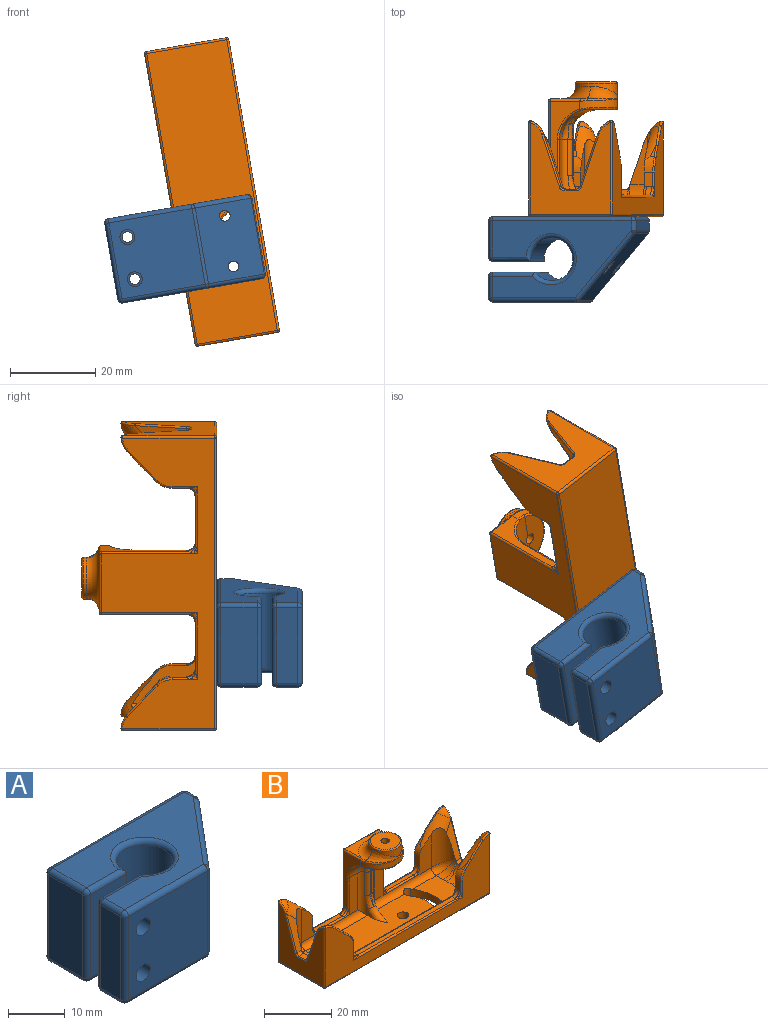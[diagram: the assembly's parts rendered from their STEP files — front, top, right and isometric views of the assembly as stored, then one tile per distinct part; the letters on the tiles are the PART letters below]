
ASSEMBLY  parts=2 mates=1
PART A: 56 faces, bbox 35.6x20.6x20.6 mm
  f0: plane 18x5.02mm, normal (-1,0,0), area 90.4mm2, adj f44,f49,f52,f55
  f1: plane 19.74x18mm, normal (0,-1,0), area 336mm2, adj f13,f14,f41,f50,f51,f55
  f2: plane 18.63x16.41mm, normal (0.77,-0.64,0), area 355.8mm2, adj f15,f16,f32,f40,f41,f42
  f3: plane 18x2.22mm, normal (1,0,0), area 40mm2, adj f22,f31,f32,f33
  f4: plane 33x18mm, normal (0,1,0), area 574.4mm2, adj f11,f12,f15,f16,f17,f21,f22,f23
  f5: plane 18x8.48mm, normal (-1,0,0), area 152.6mm2, adj f17,f20,f24,f25
  f6: plane 18x9.02mm, normal (0,-1,0), area 152.6mm2, adj f7,f11,f12,f25,f30,f34
  f7: cylinder r=5mm len=18mm, axis (0,0,-1), area 516.7mm2, adj f6,f8,f35,f38
  f8: plane 18x9.98mm, normal (0,1,0), area 160.5mm2, adj f7,f13,f14,f39,f43,f44
  f9: plane 33x18mm, normal (0,0,1), area 338.4mm2, adj f20,f21,f30,f31,f35,f39,f40,f49
  f10: plane 33x18mm, normal (0,0,-1), area 338.4mm2, adj f23,f24,f33,f34,f38,f42,f43,f51
  f11: cylinder r=1.25mm len=10.48mm, axis (0,-1,0), area 82.3mm2, adj f4,f6
  f12: cylinder r=1.25mm len=10.48mm, axis (0,-1,0), area 82.3mm2, adj f4,f6
  f13: cylinder r=1.75mm len=7.02mm, axis (0,-1,0), area 77.2mm2, adj f1,f8
  f14: cylinder r=1.75mm len=7.02mm, axis (0,-1,0), area 77.2mm2, adj f1,f8
  f15: cylinder r=1.25mm len=13.4mm, axis (0,1,0), area 93.6mm2, adj f2,f4
  f16: cylinder r=1.25mm len=13.4mm, axis (0,1,0), area 93.6mm2, adj f2,f4
  f17: cylinder r=1mm len=18mm, axis (0,0,1), area 28.3mm2, adj f4,f5,f18,f19
  f18: sphere r=1mm, area 1.6mm2, adj f17,f20,f21
  f19: sphere r=1mm, area 1.6mm2, adj f17,f23,f24
  f20: cylinder r=1mm len=8.48mm, axis (0,1,0), area 13.3mm2, adj f5,f9,f18,f26
  f21: cylinder r=1mm len=33mm, axis (1,0,0), area 51.8mm2, adj f4,f9,f18,f27
  f22: cylinder r=1mm len=18mm, axis (0,0,-1), area 28.3mm2, adj f3,f4,f27,f28
  f23: cylinder r=1mm len=33mm, axis (-1,0,0), area 51.8mm2, adj f4,f10,f19,f28
  f24: cylinder r=1mm len=8.48mm, axis (0,-1,0), area 13.3mm2, adj f5,f10,f19,f29
  f25: cylinder r=1mm len=18mm, axis (0,0,-1), area 28.3mm2, adj f5,f6,f26,f29
  f26: sphere r=1mm, area 1.6mm2, adj f20,f25,f30
  f27: sphere r=1mm, area 1.6mm2, adj f21,f22,f31
  f28: sphere r=1mm, area 1.6mm2, adj f22,f23,f33
  f29: sphere r=1mm, area 1.6mm2, adj f24,f25,f34
  f30: cylinder r=1mm len=9.02mm, axis (-1,0,0), area 13.4mm2, adj f6,f9,f26,f35
  f31: cylinder r=1mm len=2.22mm, axis (0,-1,0), area 3.5mm2, adj f3,f9,f27,f36
  f32: cylinder r=1mm len=18mm, axis (0,0,1), area 12.6mm2, adj f2,f3,f36,f37
  f33: cylinder r=1mm len=2.22mm, axis (0,1,0), area 3.5mm2, adj f3,f10,f28,f37
  f34: cylinder r=1mm len=9.02mm, axis (1,0,0), area 13.4mm2, adj f6,f10,f29,f38
  f35: torus R=6mm, axis (0,0,1), area 47.2mm2, adj f7,f9,f30,f39
  f36: sphere r=1mm, area 1mm2, adj f31,f32,f40
  f37: sphere r=1mm, area 1mm2, adj f32,f33,f42
  f38: torus R=6mm, axis (0,0,1), area 47.2mm2, adj f7,f10,f34,f43
  f39: cylinder r=1mm len=9.98mm, axis (1,0,0), area 15.3mm2, adj f8,f9,f35,f45
  f40: cylinder r=1mm len=16.42mm, axis (-0.64,-0.77,0), area 32.4mm2, adj f2,f9,f36,f46
  f41: cylinder r=1mm len=18mm, axis (0,0,-1), area 15.7mm2, adj f1,f2,f46,f47
  f42: cylinder r=1mm len=16.42mm, axis (0.64,0.77,0), area 32.4mm2, adj f2,f10,f37,f47
  f43: cylinder r=1mm len=9.98mm, axis (-1,0,0), area 15.3mm2, adj f8,f10,f38,f48
  f44: cylinder r=1mm len=18mm, axis (0,0,1), area 28.3mm2, adj f0,f8,f45,f48
  f45: sphere r=1mm, area 1.6mm2, adj f39,f44,f49
  f46: sphere r=1mm, area 0.6mm2, adj f40,f41,f50
  f47: sphere r=1mm, area 0.9mm2, adj f41,f42,f51
  f48: sphere r=1mm, area 1.6mm2, adj f43,f44,f52
  f49: cylinder r=1mm len=5.02mm, axis (0,1,0), area 7.9mm2, adj f0,f9,f45,f53
  f50: cylinder r=1mm len=19.74mm, axis (-1,0,0), area 31mm2, adj f1,f9,f46,f53
  f51: cylinder r=1mm len=19.74mm, axis (1,0,0), area 31mm2, adj f1,f10,f47,f54
  f52: cylinder r=1mm len=5.02mm, axis (0,-1,0), area 7.9mm2, adj f0,f10,f48,f54
  f53: sphere r=1mm, area 1.6mm2, adj f49,f50,f55
  f54: sphere r=1mm, area 1.6mm2, adj f51,f52,f55
  f55: cylinder r=1mm len=18mm, axis (0,0,-1), area 28.3mm2, adj f0,f1,f53,f54
PART B: 212 faces, bbox 74x22.6x33.9 mm
  f0: cylinder r=2mm len=2mm, axis (0,-1,0), area 3.9mm2, adj f28,f31,f208,f209
  f1: cylinder r=2mm len=2mm, axis (0,1,0), area 3.9mm2, adj f30,f35,f206,f207
  f2: cylinder r=2mm len=2mm, axis (0,-1,0), area 3mm2, adj f3,f27,f37,f211
  f3: bspline ~2.19x2.14mm, area 2mm2, adj f2,f8,f27,f37,f137,f192
  f4: cylinder r=2mm len=2mm, axis (0,1,0), area 3mm2, adj f5,f28,f38,f210
  f5: bspline ~2.17x2.17mm, area 1.9mm2, adj f4,f7,f28,f38,f119,f122
  f6: bspline ~1.67x1.66mm, area 0.8mm2, adj f125,f128,f211
  f7: bspline ~1.84x1.84mm, area 0.8mm2, adj f5,f119,f122
  f8: bspline ~1.72x1.68mm, area 0.7mm2, adj f3,f137,f192
  f9: bspline ~1.72x1.68mm, area 0.7mm2, adj f134,f198,f210
  f10: bspline ~1.72x1.68mm, area 0.7mm2, adj f119,f191,f209
  f11: bspline ~1.72x1.68mm, area 0.7mm2, adj f135,f150,f207
  f12: bspline ~1.72x1.68mm, area 0.7mm2, adj f135,f171,f205
  f13: bspline ~1.72x1.68mm, area 0.7mm2, adj f125,f170,f202
  f14: plane 13.5x3.6mm, normal (0,-1,0), area 48.6mm2, adj f58,f60,f61,f192
  f15: plane 12.4x7.12mm, normal (0,-1,0), area 51.8mm2, adj f31,f62,f89,f97,f99,f208
  f16: plane 12x10.12mm, normal (0,0,1), area 100.1mm2, adj f62,f83,f84,f85,f86,f87,f111,f114
  f17: plane 0.3x0.1mm, normal (-1,0,0), area 0mm2, adj f43,f87,f89
  f18: plane 11.44x4.12mm, normal (1,0,0), area 24.5mm2, adj f40,f76,f102,f113
  f19: plane 12.4x7.12mm, normal (0,-1,0), area 51.8mm2, adj f34,f60,f82,f103,f104,f200
  f20: plane 44.84x12.37mm, normal (0,0,1), area 492.7mm2, adj f55,f56,f60,f62,f71,f76,f77,f78
  f21: plane 69x26.5mm, normal (0,1,0), area 899.8mm2, adj f119,f122,f125,f128,f129,f143,f147,f149
  f22: plane 21.43x19mm, normal (-1,0,0), area 244.6mm2, adj f140,f146,f149,f156,f157,f158,f159,f160
  f23: plane 69x21.46mm, normal (0,-1,0), area 584.8mm2, adj f135,f138,f140,f141,f150,f151,f152,f153
  f24: plane 21.43x19mm, normal (1,0,0), area 244.6mm2, adj f138,f142,f143,f177,f178,f179,f180,f181
  f25: plane 69x19mm, normal (0,0,-1), area 1255.1mm2, adj f114,f115,f116,f117,f118,f141,f142,f146
  f26: plane 13.5x3.6mm, normal (0,-1,0), area 48.6mm2, adj f58,f62,f64,f198
  f27: plane 11.03x1.53mm, normal (0,0,1), area 16.5mm2, adj f2,f3,f125,f137,f201,f202,f211
  f28: plane 11.03x1.53mm, normal (0,0,1), area 16.5mm2, adj f0,f4,f5,f119,f134,f209,f210
  f29: plane 63x16.19mm, normal (0,1,0), area 270.1mm2, adj f32,f35,f94,f95,f100,f102,f109,f110
  f30: plane 41x1.5mm, normal (0,0,1), area 61.5mm2, adj f1,f135,f136,f204,f205,f207
  f31: plane 3.52x2.14mm, normal (-1,0,0), area 7.2mm2, adj f0,f15,f97,f191,f208,f209
  f32: plane 3.52x2.14mm, normal (-1,0,0), area 7.2mm2, adj f29,f94,f171,f203,f204,f205
  f33: plane 11.44x4.12mm, normal (-1,0,0), area 24.5mm2, adj f45,f83,f95,f109
  f34: plane 3.52x2.14mm, normal (1,0,0), area 7.2mm2, adj f19,f103,f170,f200,f201,f202
  f35: plane 3.52x2.14mm, normal (1,0,0), area 7.2mm2, adj f1,f29,f100,f150,f206,f207
  f36: plane 0.3x0.1mm, normal (1,0,0), area 0mm2, adj f42,f80,f82
  f37: plane 20.04x7.04mm, normal (-1,0,0), area 52.2mm2, adj f2,f3,f50,f128,f133,f192,f193,f211
  f38: plane 20.14x7.04mm, normal (1,0,0), area 52.2mm2, adj f4,f5,f50,f120,f121,f122,f123,f197
  f39: plane 14x7.02mm, normal (0,0,1), area 39.9mm2, adj f106,f123,f129,f132,f133
  f40: plane 12.88x4.42mm, normal (0,0.95,0.32), area 24.6mm2, adj f18,f77,f78,f91,f102,f158
  f41: plane 2.57x2.1mm, normal (0,0,1), area 5.4mm2, adj f78,f90,f91,f160
  f42: plane 12.99x4.53mm, normal (0,-0.95,0.32), area 27.6mm2, adj f36,f78,f79,f82,f90,f104,f162
  f43: plane 12.99x4.53mm, normal (0,-0.95,0.32), area 27.6mm2, adj f17,f85,f86,f89,f92,f99,f183
  f44: plane 2.57x2.1mm, normal (0,0,1), area 5.4mm2, adj f85,f92,f93,f181
  f45: plane 12.88x4.42mm, normal (0,0.95,0.32), area 24.6mm2, adj f33,f84,f85,f93,f95,f179
  f46: plane 13.63x5.1mm, normal (0,0,-1), area 47.5mm2, adj f48,f58,f195
  f47: cylinder r=4.9mm len=9.8mm, axis (0,0,-1), area 37.4mm2, adj f106,f107,f108,f199
  f48: cylinder r=1.25mm len=6.5mm, axis (0,0,-1), area 51.1mm2, adj f46,f49,f58
  f49: plane 9x9mm, normal (0,0,1), area 58.7mm2, adj f48,f199
  f50: cylinder r=7.5mm len=15mm, axis (0,0,1), area 44.4mm2, adj f37,f38,f124,f127,f130,f132,f194,f195
  f51: plane 2.72x2.72mm, normal (-0.71,0,0.71), area 1.8mm2, adj f94,f95,f173
  f52: plane 2.72x2.72mm, normal (-0.71,0,0.71), area 1.8mm2, adj f97,f99,f189
  f53: plane 2.72x2.72mm, normal (0.71,0,0.71), area 1.8mm2, adj f100,f102,f152
  f54: plane 2.72x2.72mm, normal (0.71,0,0.71), area 1.8mm2, adj f103,f104,f168
  f55: plane 2.18x2.18mm, normal (-1,0,0), area 2.1mm2, adj f20,f61,f71
  f56: plane 2.18x2.18mm, normal (1,0,0), area 2.1mm2, adj f20,f64,f71
  f57: plane 12.5x2.39mm, normal (0,-1,0), area 10.4mm2, adj f59,f65,f68,f69,f73,f74
  f58: cylinder r=7mm len=14.2mm, axis (-1,0,0), area 108.9mm2, adj f14,f26,f46,f48,f63,f65,f66,f193
  f59: cylinder r=7mm len=3.97mm, axis (-1,0,0), area 1.4mm2, adj f57,f70,f72
  f60: cylinder r=2mm len=26mm, axis (1,0,0), area 78.5mm2, adj f14,f19,f20,f61,f81,f137
  f61: cylinder r=2mm len=15.5mm, axis (0,0,1), area 35.9mm2, adj f14,f55,f60,f63,f72,f73
  f62: cylinder r=2mm len=26mm, axis (1,0,0), area 76.1mm2, adj f15,f16,f20,f26,f64,f88,f115,f116
  f63: torus R=5mm, axis (1,0,0), area 8.7mm2, adj f58,f61,f74,f75
  f64: cylinder r=2mm len=15.5mm, axis (0,0,-1), area 35.9mm2, adj f26,f56,f62,f66,f69,f70
  f65: cylinder r=2mm len=7mm, axis (-1,0,0), area 8.7mm2, adj f57,f58,f67,f75
  f66: torus R=5mm, axis (1,0,0), area 8.7mm2, adj f58,f64,f67,f68
  f67: bspline ~2.42x2.34mm, area 1.2mm2, adj f65,f66,f68
  f68: bspline ~5.73x2.08mm, area 5.9mm2, adj f57,f66,f67,f69
  f69: cylinder r=1.5mm len=8.5mm, axis (0,0,-1), area 14.4mm2, adj f57,f64,f68,f70
  f70: bspline ~7.01x2.35mm, area 8.6mm2, adj f59,f64,f69,f71
  f71: torus R=8.5mm, axis (1,0,0), area 23.3mm2, adj f20,f55,f56,f70,f72
  f72: bspline ~6.14x2.35mm, area 8.6mm2, adj f59,f61,f71,f73
  f73: cylinder r=1.5mm len=8.5mm, axis (0,0,1), area 14.4mm2, adj f57,f61,f72,f74
  f74: bspline ~5.33x2.08mm, area 5.9mm2, adj f57,f63,f73,f75
  f75: bspline ~2.8x2.75mm, area 1.2mm2, adj f63,f65,f74
  f76: cylinder r=5mm len=5mm, axis (0,1,0), area 32.2mm2, adj f18,f20,f77,f112
  f77: bspline ~5.08x5.07mm, area 7.3mm2, adj f20,f40,f76,f78
  f78: cylinder r=5mm len=4.98mm, axis (0,-1,0), area 21.5mm2, adj f20,f40,f41,f42,f77,f79,f90,f91
  f79: bspline ~5x5mm, area 7.5mm2, adj f20,f42,f78,f80
  f80: cylinder r=5mm len=5mm, axis (0,1,0), area 15.8mm2, adj f20,f36,f79,f81
  f81: bspline ~5.23x5mm, area 10.8mm2, adj f60,f80,f82
  f82: cylinder r=5mm len=13.53mm, axis (0,0,-1), area 77.4mm2, adj f19,f36,f42,f81,f104
  f83: cylinder r=5mm len=5mm, axis (0,-1,0), area 32.2mm2, adj f16,f33,f84,f110
  f84: bspline ~5.08x5.07mm, area 7.3mm2, adj f16,f45,f83,f85
  f85: cylinder r=5mm len=4.98mm, axis (0,-1,0), area 21.5mm2, adj f16,f43,f44,f45,f84,f86,f92,f93
  f86: bspline ~5x5mm, area 7.5mm2, adj f16,f43,f85,f87
  f87: cylinder r=5mm len=5mm, axis (0,-1,0), area 15.8mm2, adj f16,f17,f86,f88
  f88: bspline ~5.91x5mm, area 10.8mm2, adj f62,f87,f89
  f89: cylinder r=5mm len=13.53mm, axis (0,0,1), area 77.4mm2, adj f15,f17,f43,f88,f99
  f90: cylinder r=1mm len=2.1mm, axis (-1,0,0), area 2.5mm2, adj f41,f42,f78,f161
  f91: cylinder r=1mm len=2.1mm, axis (1,0,0), area 2.5mm2, adj f40,f41,f78,f159
  f92: cylinder r=1mm len=2.1mm, axis (-1,0,0), area 2.5mm2, adj f43,f44,f85,f182
  f93: cylinder r=1mm len=2.1mm, axis (1,0,0), area 2.5mm2, adj f44,f45,f85,f180
  f94: cylinder r=5mm len=3.54mm, axis (0,-1,0), area 7.7mm2, adj f29,f32,f51,f95,f172
  f95: cylinder r=5mm len=11.54mm, axis (0.69,-0.23,0.69), area 27.7mm2, adj f29,f33,f45,f51,f94,f96,f109,f174
  f96: sphere r=5mm, area 7.8mm2, adj f95,f175,f176,f177
  f97: cylinder r=5mm len=3.54mm, axis (0,-1,0), area 7.7mm2, adj f15,f31,f52,f99,f190
  f98: sphere r=5mm, area 7.8mm2, adj f99,f185,f186,f187
  f99: cylinder r=5mm len=11.54mm, axis (-0.69,-0.23,-0.69), area 35.5mm2, adj f15,f43,f52,f89,f97,f98,f184,f188
  f100: cylinder r=5mm len=3.54mm, axis (0,1,0), area 7.7mm2, adj f29,f35,f53,f102,f151
  f101: sphere r=5mm, area 7.8mm2, adj f102,f154,f155,f156
  f102: cylinder r=5mm len=11.54mm, axis (-0.69,-0.23,0.69), area 27.7mm2, adj f18,f29,f40,f53,f100,f101,f113,f153
  f103: cylinder r=5mm len=3.54mm, axis (0,1,0), area 7.7mm2, adj f19,f34,f54,f104,f169
  f104: cylinder r=5mm len=11.54mm, axis (0.69,-0.23,-0.69), area 35.5mm2, adj f19,f42,f54,f82,f103,f105,f163,f167
  f105: sphere r=5mm, area 7.8mm2, adj f104,f164,f165,f166
  f106: torus R=7.9mm, axis (0,0,1), area 71mm2, adj f39,f47,f107,f108,f120,f130
  f107: bspline ~3.07x2.71mm, area 3.3mm2, adj f47,f106,f108,f121,f124
  f108: bspline ~14.06x7.35mm, area 39.9mm2, adj f47,f106,f107,f127
  f109: cylinder r=1mm len=12.19mm, axis (0,0,1), area 18.5mm2, adj f29,f33,f95,f110
  f110: torus R=4mm, axis (0,-1,0), area 11.4mm2, adj f29,f83,f109,f111
  f111: cylinder r=1mm len=55mm, axis (-1,0,0), area 86.2mm2, adj f16,f20,f29,f110,f112,f114
  f112: torus R=4mm, axis (0,-1,0), area 11.4mm2, adj f29,f76,f111,f113
  f113: cylinder r=1mm len=12.19mm, axis (0,0,-1), area 18.5mm2, adj f18,f29,f102,f112
  f114: cylinder r=1.75mm len=3.45mm, axis (0,0,1), area 13.7mm2, adj f16,f20,f25,f111,f115,f117
  f115: cylinder r=13.75mm len=11.42mm, axis (0,0,1), area 30mm2, adj f16,f25,f62,f114,f116
  f116: cylinder r=1.75mm len=3.17mm, axis (0,0,1), area 13.9mm2, adj f20,f25,f62,f115,f117
  f117: cylinder r=10.25mm len=8.51mm, axis (0,0,1), area 22.4mm2, adj f20,f25,f114,f116
  f118: cylinder r=1.75mm len=3.5mm, axis (0,0,1), area 27.5mm2, adj f20,f25
  f119: cylinder r=0.5mm len=15.9mm, axis (-1,0,0), area 10.2mm2, adj f5,f7,f10,f21,f28,f209
  f120: bspline ~3.06x0.63mm, area 0.8mm2, adj f38,f106,f121,f123
  f121: bspline ~2.08x0.58mm, area 0.6mm2, adj f38,f107,f120,f124
  f122: cylinder r=0.5mm len=22.5mm, axis (0,0,1), area 16.5mm2, adj f5,f7,f21,f38,f126
  f123: cylinder r=0.5mm len=5.01mm, axis (0,-1,0), area 3.9mm2, adj f38,f39,f120,f126
  f124: bspline ~1.43x0.54mm, area 0.1mm2, adj f50,f107,f121,f127
  f125: cylinder r=0.5mm len=15.9mm, axis (-1,0,0), area 10.2mm2, adj f6,f13,f21,f27,f202,f211
  f126: sphere r=0.5mm, area 0.2mm2, adj f122,f123,f129
  f127: bspline ~15.02x8.14mm, area 7.9mm2, adj f50,f108,f124,f130
  f128: cylinder r=0.5mm len=22.5mm, axis (0,0,-1), area 16.5mm2, adj f6,f21,f37,f131,f211
  f129: cylinder r=0.5mm len=14mm, axis (-1,0,0), area 11mm2, adj f21,f39,f126,f131
  f130: bspline ~4.88x1.03mm, area 1.2mm2, adj f50,f106,f127,f132
  f131: sphere r=0.5mm, area 0.5mm2, adj f128,f129,f133
  f132: torus R=7mm, axis (0,0,1), area 0mm2, adj f39,f50,f130,f133
  f133: cylinder r=0.5mm len=7mm, axis (0,1,0), area 5.5mm2, adj f37,f39,f131,f132
  f134: cylinder r=0.5mm len=13.4mm, axis (-1,0,0), area 9.4mm2, adj f9,f28,f62,f208,f210
  f135: cylinder r=0.5mm len=45.8mm, axis (1,0,0), area 33.7mm2, adj f11,f12,f23,f30,f205,f207
  f136: cylinder r=0.5mm len=41mm, axis (1,0,0), area 32.2mm2, adj f29,f30,f203,f206
  f137: cylinder r=0.5mm len=13.4mm, axis (-1,0,0), area 9.4mm2, adj f3,f8,f27,f60,f200
  f138: cylinder r=0.5mm len=21.46mm, axis (0,0,-1), area 16.8mm2, adj f23,f24,f139,f176
  f139: sphere r=0.5mm, area 0.4mm2, adj f138,f141,f142
  f140: cylinder r=0.5mm len=21.46mm, axis (0,0,1), area 16.8mm2, adj f22,f23,f144,f155
  f141: cylinder r=0.5mm len=69mm, axis (-1,0,0), area 54.2mm2, adj f23,f25,f139,f144
  f142: cylinder r=0.5mm len=19mm, axis (0,-1,0), area 14.9mm2, adj f24,f25,f139,f145
  f143: cylinder r=0.5mm len=21.46mm, axis (0,0,1), area 16.8mm2, adj f21,f24,f145,f186
  f144: sphere r=0.5mm, area 0.4mm2, adj f140,f141,f146
  f145: sphere r=0.5mm, area 0.2mm2, adj f142,f143,f147
  f146: cylinder r=0.5mm len=19mm, axis (0,1,0), area 14.9mm2, adj f22,f25,f144,f148
  f147: cylinder r=0.5mm len=69mm, axis (1,0,0), area 54.2mm2, adj f21,f25,f145,f148
  f148: sphere r=0.5mm, area 0.5mm2, adj f146,f147,f149
  f149: cylinder r=0.5mm len=21.46mm, axis (0,0,-1), area 16.8mm2, adj f21,f22,f148,f165
  f150: cylinder r=0.4mm len=5.93mm, axis (0,0,1), area 2.8mm2, adj f11,f23,f35,f151,f207
  f151: torus R=4.6mm, axis (0,-1,0), area 2.4mm2, adj f23,f100,f150,f152
  f152: cylinder r=0.4mm len=3mm, axis (-0.71,0,0.71), area 2.4mm2, adj f23,f53,f151,f153
  f153: bspline ~8.85x8.52mm, area 4.7mm2, adj f23,f102,f152,f154
  f154: torus R=4.34mm, axis (0,-1,0), area 2.3mm2, adj f23,f101,f153,f155
  f155: bspline ~0.75x0.7mm, area 0.4mm2, adj f101,f140,f154,f156
  f156: torus R=4.6mm, axis (-1,0,0), area 2.7mm2, adj f22,f101,f155,f157
  f157: bspline ~1.55x0.91mm, area 0.1mm2, adj f22,f102,f156,f158
  f158: cylinder r=0.4mm len=12.27mm, axis (0,0.32,-0.95), area 8.1mm2, adj f22,f40,f157,f159
  f159: torus R=1.4mm, axis (-1,0,0), area 0.9mm2, adj f22,f91,f158,f160
  f160: cylinder r=0.4mm len=2.57mm, axis (0,1,0), area 1.6mm2, adj f22,f41,f159,f161
  f161: torus R=1.4mm, axis (-1,0,0), area 0.9mm2, adj f22,f90,f160,f162
  f162: cylinder r=0.4mm len=12.27mm, axis (0,0.32,0.95), area 8.1mm2, adj f22,f42,f161,f163
  f163: bspline ~1.55x0.91mm, area 0.1mm2, adj f22,f104,f162,f164
  f164: torus R=4.6mm, axis (-1,0,0), area 2.7mm2, adj f22,f105,f163,f165
  f165: bspline ~0.7x0.67mm, area 0.4mm2, adj f105,f149,f164,f166
  f166: torus R=4.34mm, axis (0,-1,0), area 2.3mm2, adj f21,f105,f165,f167
  f167: bspline ~8.85x8.52mm, area 4.7mm2, adj f21,f104,f166,f168
  f168: cylinder r=0.4mm len=3mm, axis (0.71,0,-0.71), area 2.4mm2, adj f21,f54,f167,f169
  f169: torus R=4.6mm, axis (0,-1,0), area 2.4mm2, adj f21,f103,f168,f170
  f170: cylinder r=0.4mm len=5.93mm, axis (0,0,1), area 2.8mm2, adj f13,f21,f34,f169,f202
  f171: cylinder r=0.4mm len=5.93mm, axis (0,0,-1), area 2.8mm2, adj f12,f23,f32,f172,f205
  f172: torus R=4.6mm, axis (0,-1,0), area 2.4mm2, adj f23,f94,f171,f173
  f173: cylinder r=0.4mm len=3mm, axis (0.71,0,0.71), area 2.4mm2, adj f23,f51,f172,f174
  f174: bspline ~7.08x6.67mm, area 4.7mm2, adj f23,f95,f173,f175
  f175: torus R=4.34mm, axis (0,-1,0), area 2.3mm2, adj f23,f96,f174,f176
  f176: bspline ~0.7x0.67mm, area 0.4mm2, adj f96,f138,f175,f177
  f177: torus R=4.6mm, axis (-1,0,0), area 2.7mm2, adj f24,f96,f176,f178
  f178: bspline ~1.55x0.91mm, area 0.1mm2, adj f24,f95,f177,f179
  f179: cylinder r=0.4mm len=12.27mm, axis (0,-0.32,0.95), area 8.1mm2, adj f24,f45,f178,f180
  f180: torus R=1.4mm, axis (-1,0,0), area 0.9mm2, adj f24,f93,f179,f181
  f181: cylinder r=0.4mm len=2.57mm, axis (0,-1,0), area 1.6mm2, adj f24,f44,f180,f182
  f182: torus R=1.4mm, axis (-1,0,0), area 0.9mm2, adj f24,f92,f181,f183
  f183: cylinder r=0.4mm len=12.27mm, axis (0,-0.32,-0.95), area 8.1mm2, adj f24,f43,f182,f184
  f184: bspline ~0.44x0.41mm, area 0.1mm2, adj f24,f99,f183,f185
  f185: torus R=4.6mm, axis (-1,0,0), area 2.7mm2, adj f24,f98,f184,f186
  f186: bspline ~0.75x0.7mm, area 0.4mm2, adj f98,f143,f185,f187
  f187: torus R=4.34mm, axis (0,-1,0), area 2.3mm2, adj f21,f98,f186,f188
  f188: bspline ~8.85x8.52mm, area 4.7mm2, adj f21,f99,f187,f189
  f189: cylinder r=0.4mm len=3mm, axis (-0.71,0,-0.71), area 2.4mm2, adj f21,f52,f188,f190
  f190: torus R=4.6mm, axis (0,-1,0), area 2.4mm2, adj f21,f97,f189,f191
  f191: cylinder r=0.4mm len=5.93mm, axis (0,0,-1), area 2.8mm2, adj f10,f21,f31,f190,f209
  f192: cylinder r=0.4mm len=13.5mm, axis (0,0,-1), area 7.5mm2, adj f3,f8,f14,f37,f193
  f193: torus R=7.4mm, axis (1,0,0), area 5.8mm2, adj f37,f58,f192,f194
  f194: bspline ~3.87x1.17mm, area 1.3mm2, adj f50,f58,f193,f195
  f195: torus R=7.1mm, axis (0,0,-1), area 11.9mm2, adj f46,f50,f194,f196
  f196: bspline ~4.89x1.21mm, area 1.3mm2, adj f50,f58,f195,f197
  f197: torus R=7.4mm, axis (1,0,0), area 5.8mm2, adj f38,f58,f196,f198
  f198: cylinder r=0.4mm len=13.5mm, axis (0,0,1), area 7.5mm2, adj f9,f26,f38,f197,f210
  f199: torus R=4.5mm, axis (0,0,1), area 18.8mm2, adj f47,f49
  f200: torus R=2.5mm, axis (1,0,0), area 1.7mm2, adj f19,f34,f137,f201
  f201: cylinder r=2mm len=2mm, axis (0,1,0), area 3.9mm2, adj f27,f34,f200,f202
  f202: bspline ~2.19x2.14mm, area 2mm2, adj f13,f27,f34,f125,f170,f201
  f203: torus R=2.5mm, axis (-1,0,0), area 1.7mm2, adj f29,f32,f136,f204
  f204: cylinder r=2mm len=2mm, axis (0,-1,0), area 3.9mm2, adj f30,f32,f203,f205
  f205: bspline ~2.19x2.14mm, area 2mm2, adj f12,f30,f32,f135,f171,f204
  f206: torus R=2.5mm, axis (-1,0,0), area 1.7mm2, adj f1,f29,f35,f136
  f207: bspline ~2.19x2.14mm, area 2mm2, adj f1,f11,f30,f35,f135,f150
  f208: torus R=2.5mm, axis (1,0,0), area 1.7mm2, adj f0,f15,f31,f134
  f209: bspline ~2.19x2.14mm, area 2mm2, adj f0,f10,f28,f31,f119,f191
  f210: bspline ~2.19x2.14mm, area 2mm2, adj f4,f9,f28,f38,f134,f198
  f211: bspline ~2.17x2.17mm, area 1.9mm2, adj f2,f6,f27,f37,f125,f128
PLACE A rot(axis=(0,-1,0),9.9deg) t=(11.71,5.64,-59.17)mm
PLACE B rot(axis=(-0.64,0.54,0.54),114.5deg) t=(24.42,9.63,-17.36)mm
MATE revolute A.f16 <-> B.f115  axis (0,1,0) through (31.92,7.13,-39.42)mm
